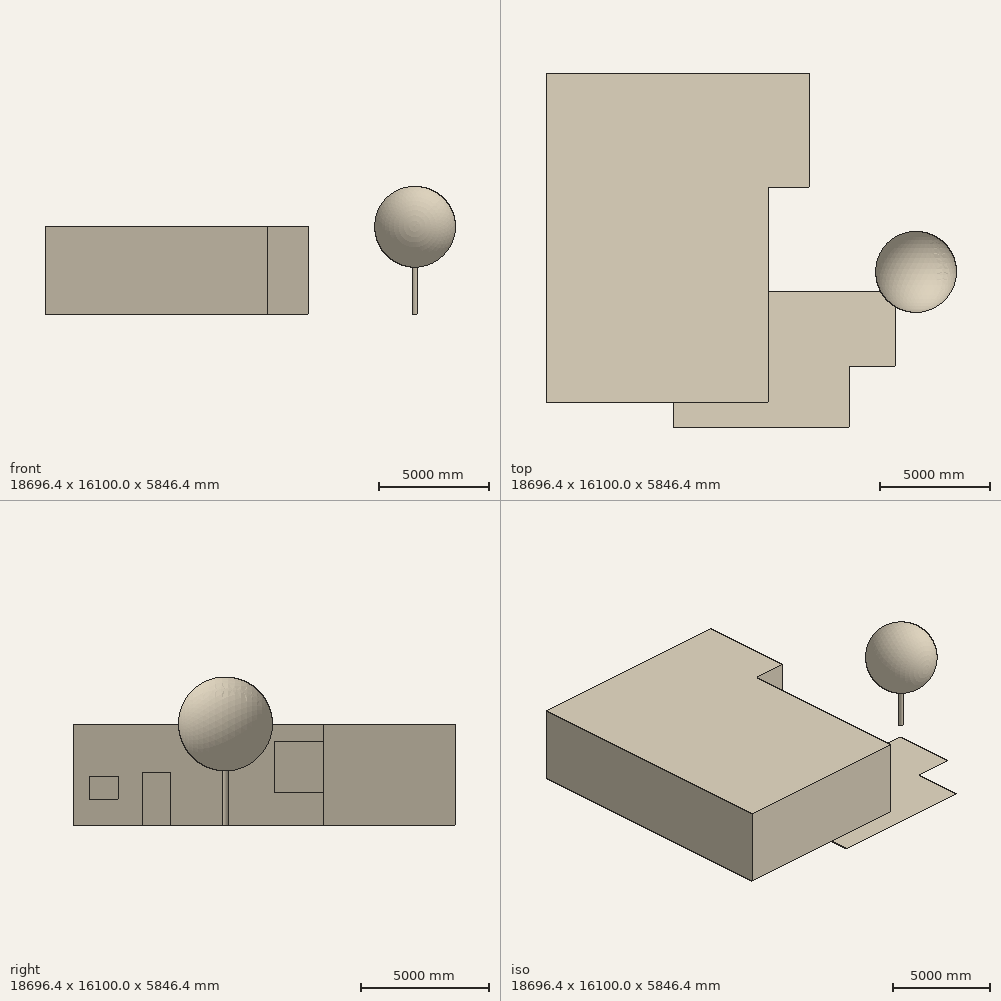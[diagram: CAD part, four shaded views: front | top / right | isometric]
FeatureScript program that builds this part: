
annotation { "Feature Type Name" : "Feature", "Feature Type Description" : "" }
export const myFeature = defineFeature(function(context is Context, id is Id, definition is map)
    precondition{}
    {
        {
            var Q0;
            Q0=qCreatedBy(makeId("Top.planeOp"),FACE);
            var sketch = newSketch(context, id + "F0", { "sketchPlane" : qUnion([Q0])});
            skLineSegment(sketch, "E0", {"start": v(1900, 5200) * mm, "end": v(1900, 0) * mm});
            skLineSegment(sketch, "E1", {"start": v(1900, 0) * mm, "end": v(0, 0) * mm});
            skLineSegment(sketch, "E2", {"start": v(0, 0) * mm, "end": v(0, -9800) * mm});
            skLineSegment(sketch, "E3", {"start": v(0, -9800) * mm, "end": v(-10100, -9800) * mm});
            skLineSegment(sketch, "E4", {"start": v(-10100, -9800) * mm, "end": v(-10100, 5200) * mm});
            skLineSegment(sketch, "E5", {"start": v(-10100, 5200) * mm, "end": v(1900, 5200) * mm});
            skSolve(sketch);
        }
        {
            var Q0;
            Q0 = qSketchRegion(id + "F0", true);
            extrude(context, id + "F1", {"entities" : qUnion([Q0]), "depth" : 4000 * mm, "offsetDistance" : 25 * mm});
        }
        {
            var Q0;
            Q0=makeQuery(id+"F1.opExtrude","SWEPT_FACE",FACE,{"disambiguationData":[OSD([sQuery(id+"F0.wireOp",EDGE,"E2")])]});
            var sketch = newSketch(context, id + "F2", { "sketchPlane" : qUnion([Q0])});
            skLineSegment(sketch, "E6.bottom", {"start": v(-1900, 3300) * mm, "end": v(0, 3300) * mm});
            skLineSegment(sketch, "E6.top", {"start": v(-1900, 1300) * mm, "end": v(0, 1300) * mm});
            skLineSegment(sketch, "E6.left", {"start": v(-1900, 3300) * mm, "end": v(-1900, 1300) * mm});
            skLineSegment(sketch, "E6.right", {"start": v(0, 3300) * mm, "end": v(0, 1300) * mm});
            skLineSegment(sketch, "E7.bottom", {"start": v(-7100, 0) * mm, "end": v(-6000, 0) * mm});
            skLineSegment(sketch, "E7.top", {"start": v(-7100, 2100) * mm, "end": v(-6000, 2100) * mm});
            skLineSegment(sketch, "E7.left", {"start": v(-7100, 0) * mm, "end": v(-7100, 2100) * mm});
            skLineSegment(sketch, "E7.right", {"start": v(-6000, 0) * mm, "end": v(-6000, 2100) * mm});
            skLineSegment(sketch, "E8.bottom", {"start": v(-9172.25, 1946.75) * mm, "end": v(-8017.25, 1946.75) * mm});
            skLineSegment(sketch, "E8.top", {"start": v(-9172.25, 1054.25) * mm, "end": v(-8017.25, 1054.25) * mm});
            skLineSegment(sketch, "E8.left", {"start": v(-8017.25, 1946.75) * mm, "end": v(-8017.25, 1054.25) * mm});
            skLineSegment(sketch, "E8.right", {"start": v(-9172.25, 1946.75) * mm, "end": v(-9172.25, 1054.25) * mm});
            skSolve(sketch);
        }
        {
            var Q0;
            Q0=makeQuery(id+"F2.imprint","IMPRINT",FACE,{"disambiguationData":[TD([[makeQuery(id+"F2.imprint","IMPRINT",EDGE,{"derivedFrom":sQuery(id+"F2.wireOp",EDGE,"E8.bottom")}),-1.0]])]});
            var Q1;
            Q1=makeQuery(id+"F2.imprint","IMPRINT",FACE,{"disambiguationData":[TD([[makeQuery(id+"F2.imprint","IMPRINT",EDGE,{"derivedFrom":sQuery(id+"F2.wireOp",EDGE,"E7.bottom")}),-1.0]])]});
            var Q2;
            Q2=makeQuery(id+"F2.imprint","IMPRINT",FACE,{"disambiguationData":[TD([[makeQuery(id+"F2.imprint","IMPRINT",EDGE,{"derivedFrom":sQuery(id+"F2.wireOp",EDGE,"E6.bottom")}),-1.0]])]});
            extrude(context, id + "F3", {"entities" : qUnion([Q0, Q1, Q2]), "operationType" : NewBodyOperationType.REMOVE, "oppositeDirection" : true, "depth" : 25 * mm, "offsetDistance" : 25 * mm});
        }
        {
            var Q0;
            Q0=qCreatedBy(makeId("Top.planeOp"),FACE);
            var sketch = newSketch(context, id + "F4", { "sketchPlane" : qUnion([Q0])});
            skCircle(sketch, "E9", {"center": v(9400.4, 2700) * mm, "radius": 3200.4 * mm});
            skSolve(sketch);
        }
        {
            var Q0;
            Q0=qCreatedBy(makeId("Top.planeOp"),FACE);
            var sketch = newSketch(context, id + "F5", { "sketchPlane" : qUnion([Q0])});
            skLineSegment(sketch, "E10", {"start": v(0, -4700) * mm, "end": v(5800, -4700) * mm});
            skLineSegment(sketch, "E11", {"start": v(5800, -4700) * mm, "end": v(5800, -8150) * mm});
            skLineSegment(sketch, "E12", {"start": v(5800, -8150) * mm, "end": v(3700, -8150) * mm});
            skLineSegment(sketch, "E13", {"start": v(3700, -8150) * mm, "end": v(3700, -10900) * mm});
            skLineSegment(sketch, "E14", {"start": v(3700, -10900) * mm, "end": v(-4300, -10900) * mm});
            skLineSegment(sketch, "E15", {"start": v(-4300, -10900) * mm, "end": v(-4300, -9800) * mm});
            skLineSegment(sketch, "E16", {"start": v(-4300, -9800) * mm, "end": v(0, -9800) * mm});
            skLineSegment(sketch, "E17", {"start": v(0, -9800) * mm, "end": v(0, -4700) * mm});
            skSolve(sketch);
        }
        {
            var Q0;
            Q0 = qSketchRegion(id + "F5", true);
            extrude(context, id + "F6", {"entities" : qUnion([Q0]), "depth" : 10 * mm, "offsetDistance" : 25 * mm});
        }
        {
            var Q0;
            Q0=qCreatedBy(makeId("Top.planeOp"),FACE);
            var sketch = newSketch(context, id + "F7", { "sketchPlane" : qUnion([Q0])});
            skCircle(sketch, "E18", {"center": v(6750, -3830) * mm, "radius": 127 * mm});
            skLineSegment(sketch, "E19", {"start": v(6750, -3830) * mm, "end": v(0, -3830) * mm, "construction": true});
            skLineSegment(sketch, "E20", {"start": v(0, 0) * mm, "end": v(0, -3830) * mm});
            skSolve(sketch);
        }
        {
            var Q0;
            Q0 = qSketchRegion(id + "F7", true);
            extrude(context, id + "F8", {"entities" : qUnion([Q0]), "depth" : 4000 * mm, "offsetDistance" : 25 * mm});
        }
        {
            var Q0;
            Q0=makeQuery(id+"F8.opExtrude","CAP_FACE",FACE,{"disambiguationData":[OSD([sQuery(id+"F7.wireOp",EDGE,"E18")])],"isStart":false});
            var sketch = newSketch(context, id + "F9", { "sketchPlane" : qUnion([Q0])});
            skLineSegment(sketch, "E21", {"start": v(6750, -3830) * mm, "end": v(6750, -1983.58) * mm});
            skLineSegment(sketch, "E22", {"start": v(6750, -3830) * mm, "end": v(6750, -5676.42) * mm});
            skArc(sketch, "E23", {"start": v(6750, -5676.42) * mm, "mid": v(8596.42, -3830) * mm, "end": v(6750, -1983.58) * mm});
            skSolve(sketch);
        }
        {
            var Q0;
            {var subQ0=sQuery(id+"F9.wireOp",EDGE,"E23");Q0=makeQuery(id+"F9.imprint","IMPRINT",FACE,{"disambiguationData":[TD([[makeQuery(id+"F9.imprint","IMPRINT",EDGE,{"derivedFrom":subQ0}),1.0]])]});}
            var Q1;
            Q1=sQuery(id+"F9.wireOp",EDGE,"E21");
            revolve(context, id + "F10", {"operationType" : NewBodyOperationType.ADD, "surfaceOperationType" : NewSurfaceOperationType.NEW, "entities" : qUnion([Q0]), "axis" : qUnion([Q1]), "revolveType" : RevolveType.FULL});
        }
    });
